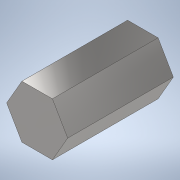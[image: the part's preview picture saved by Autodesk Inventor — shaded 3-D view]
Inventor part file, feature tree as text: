
AUTODESK INVENTOR PART (.ipt)
format: ipt  version: 2020 (Build 240168000, 168)  size: 96,256 bytes
history: native  units: in
note: dims shown in document units (in); Inventor stores cm internally (conversion verified against a paired STEP export)
features: extrude x1, sketch x1
ambient origin geometry x8: Origin, YZ Plane, XZ Plane, XY Plane, X Axis, Y Axis, Z Axis, Center Point
bodies: Solid1 (feature_tree)
feature tree (2):
  extrude  "Extrusion1"  Depth=1.0in TaperAngle=0.0deg
  sketch  "Sketch1"  dims[d0=0.5in d1=1.0in d2=0.0in]
